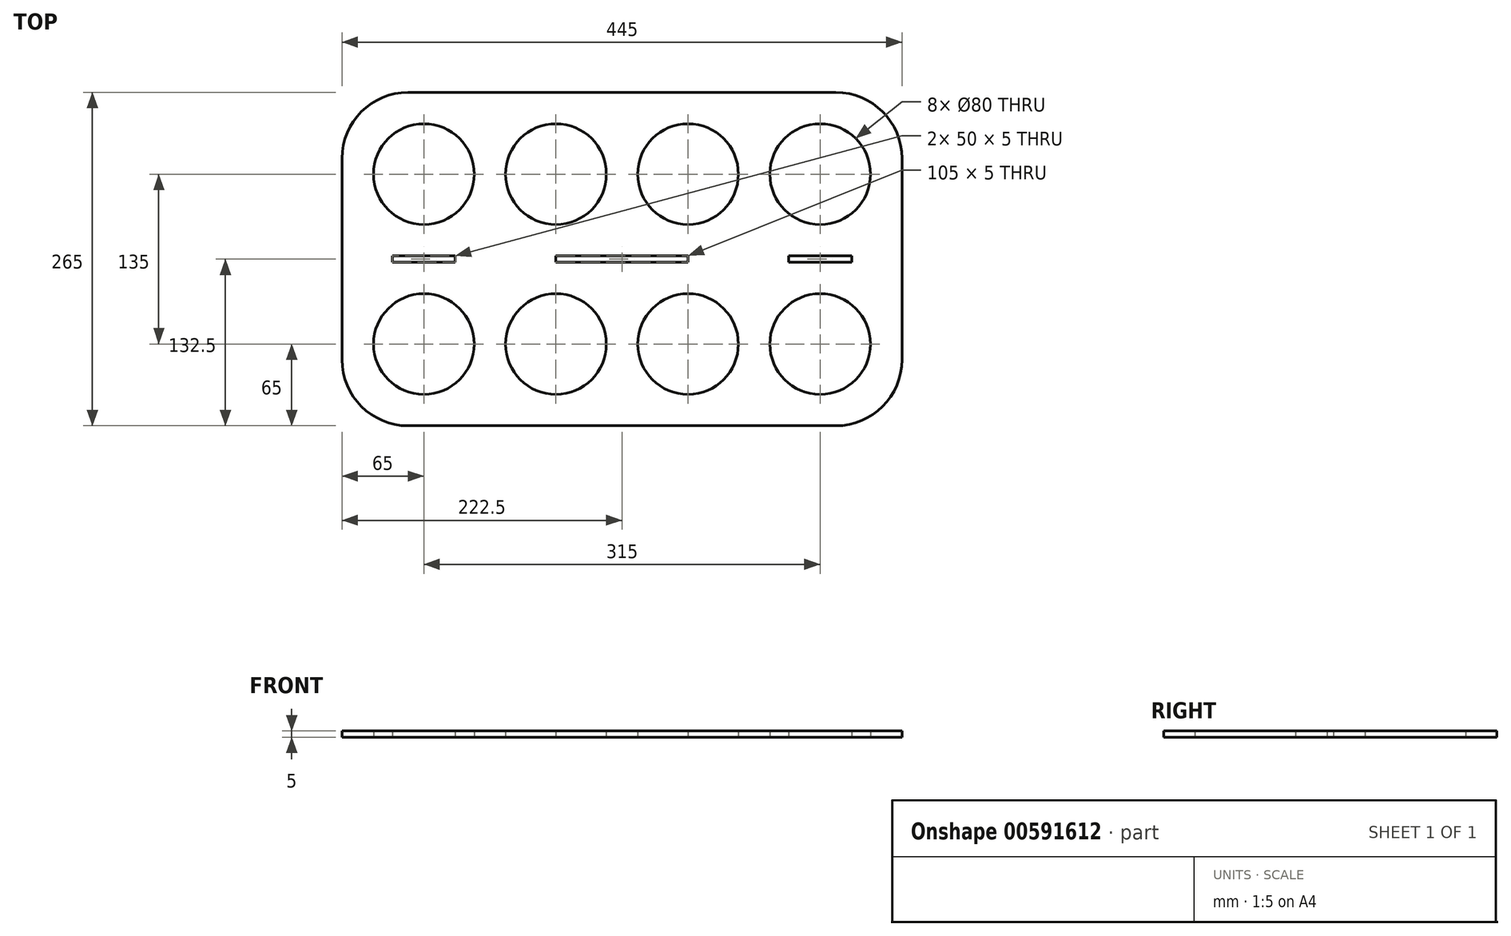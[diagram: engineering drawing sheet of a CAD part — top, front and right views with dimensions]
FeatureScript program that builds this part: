
annotation { "Feature Type Name" : "Feature", "Feature Type Description" : "" }
export const myFeature = defineFeature(function(context is Context, id is Id, definition is map)
    precondition{}
    {
        {
            var Q0;
            Q0=qCreatedBy(makeId("Top.planeOp"),FACE);
            var sketch = newSketch(context, id + "F0", { "sketchPlane" : qUnion([Q0])});
            skLineSegment(sketch, "E0.bottom", {"start": v(-233.98, 135) * mm, "end": v(81.02, 135) * mm, "construction": true});
            skLineSegment(sketch, "E0.top", {"start": v(-233.98, 0) * mm, "end": v(81.02, 0) * mm, "construction": true});
            skLineSegment(sketch, "E0.left", {"start": v(-233.98, 135) * mm, "end": v(-233.98, 0) * mm, "construction": true});
            skLineSegment(sketch, "E0.right", {"start": v(81.02, 135) * mm, "end": v(81.02, 0) * mm, "construction": true});
            skLineSegment(sketch, "E1", {"start": v(-128.98, 135) * mm, "end": v(-128.98, 0) * mm, "construction": true});
            skLineSegment(sketch, "E2", {"start": v(-23.98, 135) * mm, "end": v(-23.98, 0) * mm, "construction": true});
            skLineSegment(sketch, "E3", {"start": v(-233.98, 67.5) * mm, "end": v(81.02, 67.5) * mm, "construction": true});
            skLineSegment(sketch, "E4", {"start": v(-76.48, 135) * mm, "end": v(-76.48, 70) * mm, "construction": true});
            skCircle(sketch, "E5", {"center": v(-233.98, 135) * mm, "radius": 40 * mm});
            skCircle(sketch, "E6", {"center": v(-128.98, 135) * mm, "radius": 40 * mm});
            skCircle(sketch, "E7", {"center": v(-23.98, 135) * mm, "radius": 40 * mm});
            skCircle(sketch, "E8", {"center": v(81.02, 135) * mm, "radius": 40 * mm});
            skCircle(sketch, "E9", {"center": v(-233.98, 0) * mm, "radius": 40 * mm});
            skCircle(sketch, "E10", {"center": v(-128.98, 0) * mm, "radius": 40 * mm});
            skCircle(sketch, "E11", {"center": v(-23.98, 0) * mm, "radius": 40 * mm});
            skCircle(sketch, "E12", {"center": v(81.02, 0) * mm, "radius": 40 * mm});
            skLineSegment(sketch, "E13.bottom", {"start": v(93.52, 200) * mm, "end": v(-246.48, 200) * mm});
            skLineSegment(sketch, "E13.top", {"start": v(93.52, -65) * mm, "end": v(-246.48, -65) * mm});
            skLineSegment(sketch, "E13.left", {"start": v(146.02, 147.5) * mm, "end": v(146.02, 70) * mm});
            skLineSegment(sketch, "E13.right", {"start": v(-298.98, 147.5) * mm, "end": v(-298.98, -12.5) * mm});
            skPoint(sketch, "E13.middle", {"position": v(-76.48, 67.5) * mm});
            skPoint(sketch, "E14.visualSharp", {"position": v(-298.98, 200) * mm});
            skArc(sketch, "E14.filletArc", {"start": v(-246.48, 200) * mm, "mid": v(-283.6, 184.62) * mm, "end": v(-298.98, 147.5) * mm});
            skPoint(sketch, "E15.visualSharp", {"position": v(-298.98, -65) * mm});
            skArc(sketch, "E15.filletArc", {"start": v(-298.98, -12.5) * mm, "mid": v(-283.6, -49.62) * mm, "end": v(-246.48, -65) * mm});
            skPoint(sketch, "E16.visualSharp", {"position": v(146.02, -65) * mm});
            skArc(sketch, "E16.filletArc", {"start": v(93.52, -65) * mm, "mid": v(130.64, -49.62) * mm, "end": v(146.02, -12.5) * mm});
            skPoint(sketch, "E17.visualSharp", {"position": v(146.02, 200) * mm});
            skArc(sketch, "E17.filletArc", {"start": v(146.02, 147.5) * mm, "mid": v(130.64, 184.62) * mm, "end": v(93.52, 200) * mm});
            skPoint(sketch, "E18.right.end.orphan", {"position": v(-298.98, 65) * mm});
            skPoint(sketch, "E18.right.start.orphan", {"position": v(-298.98, 70) * mm});
            skLineSegment(sketch, "E19.trimOffspring", {"start": v(146.02, 65) * mm, "end": v(146.02, -12.5) * mm});
            skLineSegment(sketch, "E20.trimOffspring", {"start": v(-76.48, 65) * mm, "end": v(-76.48, 0) * mm, "construction": true});
            skLineSegment(sketch, "E21", {"start": v(146.02, 70) * mm, "end": v(146.02, 65) * mm});
            skLineSegment(sketch, "E22.bottom", {"start": v(-128.98, 70) * mm, "end": v(-23.98, 70) * mm});
            skLineSegment(sketch, "E22.top", {"start": v(-128.98, 65) * mm, "end": v(-23.98, 65) * mm});
            skLineSegment(sketch, "E22.left", {"start": v(-128.98, 70) * mm, "end": v(-128.98, 65) * mm});
            skLineSegment(sketch, "E22.right", {"start": v(-23.98, 70) * mm, "end": v(-23.98, 65) * mm});
            skLineSegment(sketch, "E23.bottom", {"start": v(-208.98, 70) * mm, "end": v(-258.98, 70) * mm});
            skLineSegment(sketch, "E23.top", {"start": v(-208.98, 65) * mm, "end": v(-258.98, 65) * mm});
            skLineSegment(sketch, "E23.left", {"start": v(-208.98, 70) * mm, "end": v(-208.98, 65) * mm});
            skLineSegment(sketch, "E23.right", {"start": v(-258.98, 70) * mm, "end": v(-258.98, 65) * mm});
            skPoint(sketch, "E23.middle", {"position": v(-233.98, 67.5) * mm});
            skLineSegment(sketch, "E24.bottom", {"start": v(106.02, 70) * mm, "end": v(56.02, 70) * mm});
            skLineSegment(sketch, "E24.top", {"start": v(106.02, 65) * mm, "end": v(56.02, 65) * mm});
            skLineSegment(sketch, "E24.left", {"start": v(106.02, 70) * mm, "end": v(106.02, 65) * mm});
            skLineSegment(sketch, "E24.right", {"start": v(56.02, 70) * mm, "end": v(56.02, 65) * mm});
            skPoint(sketch, "E24.middle", {"position": v(81.02, 67.5) * mm});
            skSolve(sketch);
        }
        {
            var Q0;
            Q0=qSketchRegion(id+"F0",true);
            extrude(context, id + "F1", {"entities" : qUnion([Q0]), "depth" : 5 * mm, "offsetDistance" : 25 * mm});
        }
    });
